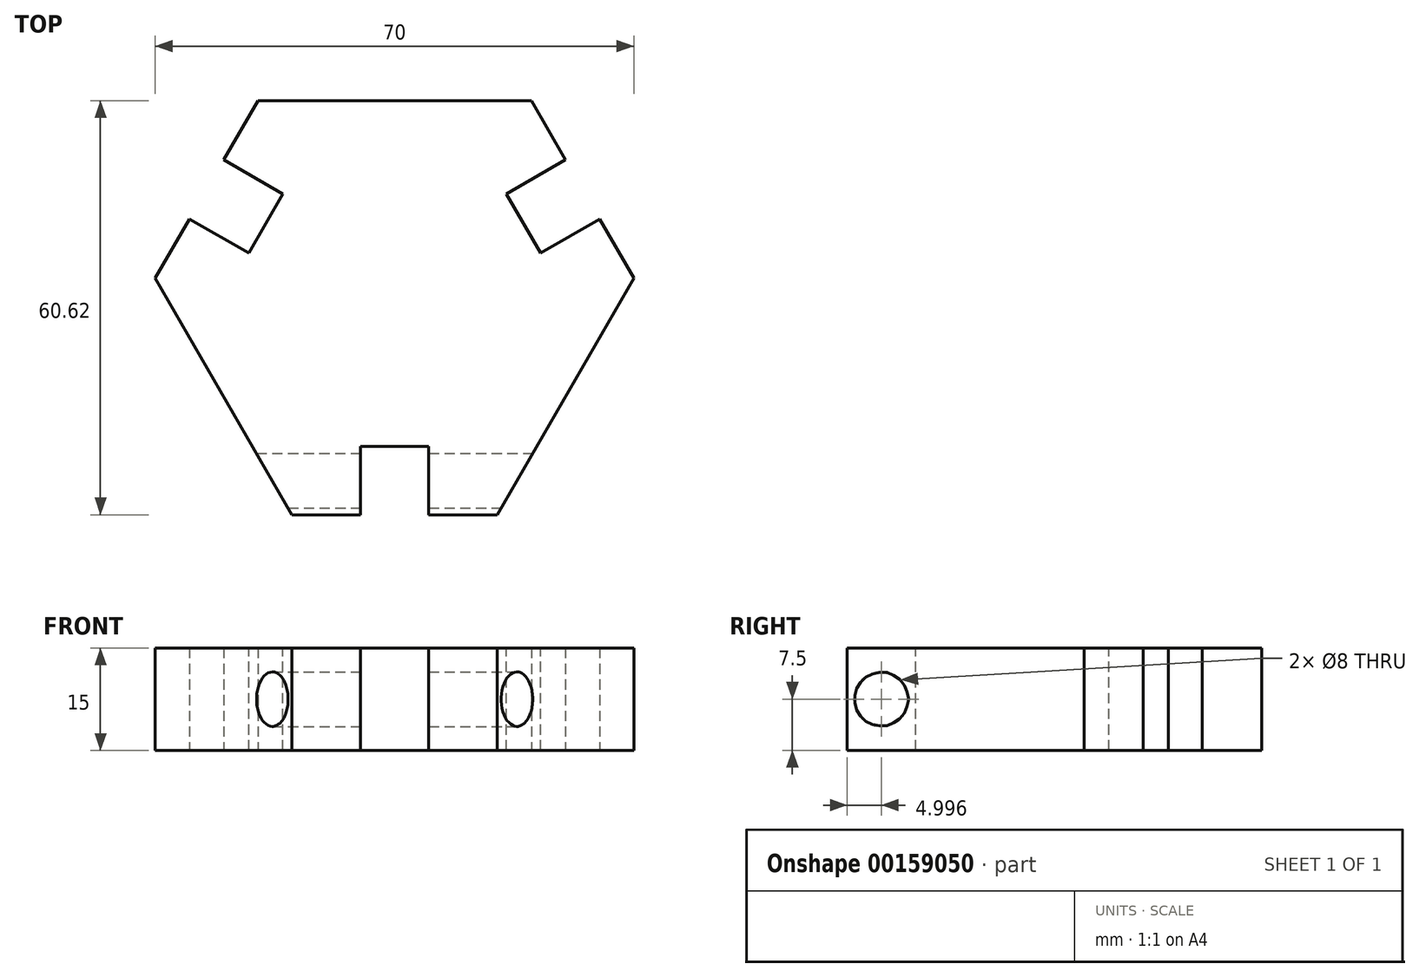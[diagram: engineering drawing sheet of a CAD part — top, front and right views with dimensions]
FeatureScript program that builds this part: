
annotation { "Feature Type Name" : "Feature", "Feature Type Description" : "" }
export const myFeature = defineFeature(function(context is Context, id is Id, definition is map)
    precondition{}
    {
        {
            var Q0;
            Q0=qCreatedBy(makeId("Top.planeOp"),FACE);
            var sketch = newSketch(context, id + "F0", { "sketchPlane" : qUnion([Q0])});
            skCircle(sketch, "E0.cCircle", {"center": v(0, 0) * mm, "radius": 28.87 * mm, "construction": true});
            skLineSegment(sketch, "E0.0", {"start": v(-50, 28.87) * mm, "end": v(50, 28.87) * mm, "construction": true});
            skLineSegment(sketch, "E0.1", {"start": v(50, 28.87) * mm, "end": v(0, -57.74) * mm, "construction": true});
            skLineSegment(sketch, "E0.2", {"start": v(0, -57.74) * mm, "end": v(-50, 28.87) * mm, "construction": true});
            skPoint(sketch, "E0.0.midPoint", {"position": v(0, 28.87) * mm});
            skLineSegment(sketch, "E1", {"start": v(-35, 2.89) * mm, "end": v(-20, 28.87) * mm});
            skLineSegment(sketch, "E2", {"start": v(-20, 28.87) * mm, "end": v(20, 28.87) * mm});
            skLineSegment(sketch, "E3", {"start": v(20, 28.87) * mm, "end": v(35, 2.89) * mm});
            skLineSegment(sketch, "E4", {"start": v(35, 2.89) * mm, "end": v(15, -31.75) * mm});
            skLineSegment(sketch, "E5", {"start": v(15, -31.75) * mm, "end": v(-15, -31.75) * mm});
            skLineSegment(sketch, "E6", {"start": v(-15, -31.75) * mm, "end": v(-35, 2.89) * mm});
            skSolve(sketch);
        }
        {
            var Q0;
            Q0 = qSketchRegion(id + "F0", true);
            extrude(context, id + "F1", {"entities" : qUnion([Q0]), "depth" : 15 * mm});
        }
        {
            var Q0;
            Q0=makeQuery(id+"F1.opExtrude","CAP_FACE",FACE,{"disambiguationData":[OSD([sQuery(id+"F0.wireOp",EDGE,"E1"),sQuery(id+"F0.wireOp",EDGE,"E2"),sQuery(id+"F0.wireOp",EDGE,"E3"),sQuery(id+"F0.wireOp",EDGE,"E4"),sQuery(id+"F0.wireOp",EDGE,"E5"),sQuery(id+"F0.wireOp",EDGE,"E6")])],"isStart":false});
            var sketch = newSketch(context, id + "F2", { "sketchPlane" : qUnion([Q0])});
            skLineSegment(sketch, "E7.bottom", {"start": v(5, -21.75) * mm, "end": v(-5, -21.75) * mm});
            skLineSegment(sketch, "E7.top", {"start": v(5, -41.75) * mm, "end": v(-5, -41.75) * mm});
            skLineSegment(sketch, "E7.left", {"start": v(5, -21.75) * mm, "end": v(5, -41.75) * mm});
            skLineSegment(sketch, "E7.right", {"start": v(-5, -21.75) * mm, "end": v(-5, -41.75) * mm});
            skPoint(sketch, "E7.middle", {"position": v(0, -31.75) * mm});
            skPoint(sketch, "E8.1.0", {"position": v(-27.5, 15.88) * mm});
            skLineSegment(sketch, "E8.1.1", {"start": v(-21.34, 6.55) * mm, "end": v(-16.34, 15.2) * mm});
            skLineSegment(sketch, "E8.1.2", {"start": v(-38.66, 16.55) * mm, "end": v(-33.66, 25.2) * mm});
            skLineSegment(sketch, "E8.1.3", {"start": v(-21.34, 6.55) * mm, "end": v(-38.66, 16.55) * mm});
            skLineSegment(sketch, "E8.1.4", {"start": v(-16.34, 15.2) * mm, "end": v(-33.66, 25.2) * mm});
            skPoint(sketch, "E8.2.0", {"position": v(27.5, 15.88) * mm});
            skLineSegment(sketch, "E8.2.1", {"start": v(16.34, 15.2) * mm, "end": v(21.34, 6.55) * mm});
            skLineSegment(sketch, "E8.2.2", {"start": v(33.66, 25.2) * mm, "end": v(38.66, 16.55) * mm});
            skLineSegment(sketch, "E8.2.3", {"start": v(16.34, 15.2) * mm, "end": v(33.66, 25.2) * mm});
            skLineSegment(sketch, "E8.2.4", {"start": v(21.34, 6.55) * mm, "end": v(38.66, 16.55) * mm});
            skPoint(sketch, "E8.center", {"position": v(0, 0) * mm});
            skLineSegment(sketch, "E8.anchor1", {"start": v(0, 0) * mm, "end": v(-5, -41.75) * mm, "construction": true});
            skLineSegment(sketch, "E8.anchor2", {"start": v(0, 0) * mm, "end": v(38.66, 16.55) * mm, "construction": true});
            skSolve(sketch);
        }
        {
            var Q0;
            Q0 = qSketchRegion(id + "F2", true);
            extrude(context, id + "F3", {"entities" : qUnion([Q0]), "operationType" : NewBodyOperationType.REMOVE, "endBound" : BoundingType.THROUGH_ALL, "oppositeDirection" : true, "depth" : 25 * mm});
        }
        {
            var Q0;
            Q0=makeQuery(id+"F3.boolean.opBoolean","COPY",FACE,{"derivedFrom":makeQuery(id+"F3.opExtrude","SWEPT_FACE",FACE,{"disambiguationData":[OSD([sQuery(id+"F2.wireOp",EDGE,"E7.right")])]})});
            var sketch = newSketch(context, id + "F4", { "sketchPlane" : qUnion([Q0])});
            skCircle(sketch, "E9", {"center": v(-26.75, 7.5) * mm, "radius": 4 * mm});
            skSolve(sketch);
        }
        {
            var Q0;
            Q0 = qSketchRegion(id + "F4", true);
            extrude(context, id + "F5", {"entities" : qUnion([Q0]), "operationType" : NewBodyOperationType.REMOVE, "endBound" : BoundingType.THROUGH_ALL, "oppositeDirection" : true, "depth" : 25 * mm, "hasSecondDirection" : true, "secondDirectionBound" : SecondDirectionBoundingType.THROUGH_ALL, "secondDirectionOppositeDirection" : false, "secondDirectionDepth" : 25 * mm});
        }
    });
